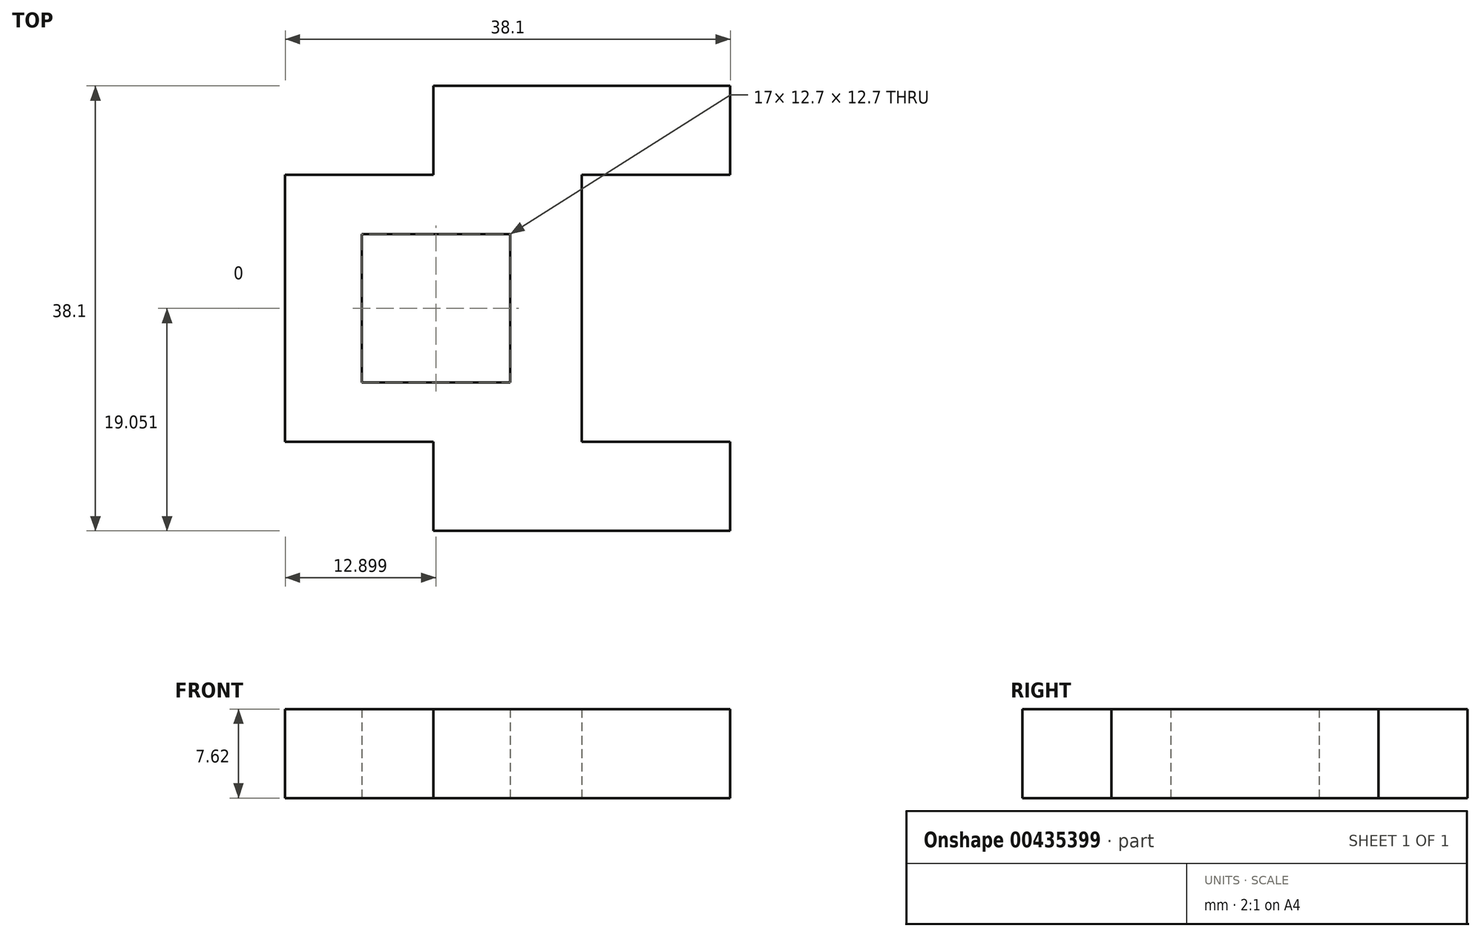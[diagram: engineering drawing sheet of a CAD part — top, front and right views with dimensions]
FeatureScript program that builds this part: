
annotation { "Feature Type Name" : "Feature", "Feature Type Description" : "" }
export const myFeature = defineFeature(function(context is Context, id is Id, definition is map)
    precondition{}
    {
        {
            var Q0;
            Q0=qCreatedBy(makeId("Top.planeOp"),FACE);
            var sketch = newSketch(context, id + "F0", { "sketchPlane" : qUnion([Q0])});
            skLineSegment(sketch, "E0.bottom", {"start": v(-69.04, 57.88) * mm, "end": v(-56.34, 57.88) * mm});
            skLineSegment(sketch, "E0.top", {"start": v(-69.04, 19.78) * mm, "end": v(-56.34, 19.78) * mm});
            skLineSegment(sketch, "E0.left", {"start": v(-69.04, 57.88) * mm, "end": v(-69.04, 45.18) * mm});
            skLineSegment(sketch, "E0.right", {"start": v(-56.34, 57.88) * mm, "end": v(-56.34, 19.78) * mm});
            skLineSegment(sketch, "E1.bottom", {"start": v(-56.34, 57.88) * mm, "end": v(-43.64, 57.88) * mm});
            skLineSegment(sketch, "E1.top", {"start": v(-56.34, 50.26) * mm, "end": v(-43.64, 50.26) * mm});
            skLineSegment(sketch, "E1.left", {"start": v(-56.34, 57.88) * mm, "end": v(-56.34, 50.26) * mm});
            skLineSegment(sketch, "E1.right", {"start": v(-43.64, 57.88) * mm, "end": v(-43.64, 50.26) * mm});
            skLineSegment(sketch, "E2.bottom", {"start": v(-56.34, 19.78) * mm, "end": v(-43.64, 19.78) * mm});
            skLineSegment(sketch, "E2.top", {"start": v(-56.34, 27.4) * mm, "end": v(-43.64, 27.4) * mm});
            skLineSegment(sketch, "E2.left", {"start": v(-56.34, 19.78) * mm, "end": v(-56.34, 27.4) * mm});
            skLineSegment(sketch, "E2.right", {"start": v(-43.64, 19.78) * mm, "end": v(-43.64, 27.4) * mm});
            skLineSegment(sketch, "E3.bottom", {"start": v(-69.04, 50.26) * mm, "end": v(-81.74, 50.26) * mm});
            skLineSegment(sketch, "E3.top", {"start": v(-69.04, 27.4) * mm, "end": v(-81.74, 27.4) * mm});
            skLineSegment(sketch, "E3.left", {"start": v(-69.04, 50.26) * mm, "end": v(-69.04, 45.18) * mm});
            skLineSegment(sketch, "E3.right", {"start": v(-81.74, 50.26) * mm, "end": v(-81.74, 27.4) * mm});
            skLineSegment(sketch, "E4.bottom", {"start": v(-75.2, 45.18) * mm, "end": v(-62.5, 45.18) * mm});
            skLineSegment(sketch, "E4.top", {"start": v(-75.2, 32.48) * mm, "end": v(-62.5, 32.48) * mm});
            skLineSegment(sketch, "E4.left", {"start": v(-75.2, 45.18) * mm, "end": v(-75.2, 45.18) * mm});
            skLineSegment(sketch, "E4.right", {"start": v(-62.5, 45.18) * mm, "end": v(-62.5, 32.48) * mm});
            skLineSegment(sketch, "E5", {"start": v(-75.2, 45.18) * mm, "end": v(-75.2, 32.48) * mm});
            skLineSegment(sketch, "E6.trimOffspring", {"start": v(-69.04, 32.48) * mm, "end": v(-69.04, 19.78) * mm});
            skLineSegment(sketch, "E7.trimOffspring", {"start": v(-69.04, 32.48) * mm, "end": v(-69.04, 27.4) * mm});
            skLineSegment(sketch, "E8", {"start": v(-62.5, 45.18) * mm, "end": v(-56.34, 45.18) * mm});
            skLineSegment(sketch, "E9", {"start": v(-62.5, 32.48) * mm, "end": v(-56.34, 32.48) * mm});
            skSolve(sketch);
        }
        {
            var Q0;
            {var subQ5=sQuery(id+"F0.wireOp",EDGE,"E3.bottom");Q0=makeQuery(id+"F0.imprint","IMPRINT",FACE,{"disambiguationData":[TD([[makeQuery(id+"F0.imprint","IMPRINT",EDGE,{"derivedFrom":subQ5}),1.0]])]});}
            var Q1;
            {var subQ9=sQuery(id+"F0.wireOp",EDGE,"E0.bottom");Q1=makeQuery(id+"F0.imprint","IMPRINT",FACE,{"disambiguationData":[TD([[makeQuery(id+"F0.imprint","IMPRINT",EDGE,{"derivedFrom":subQ9}),-1.0]])]});}
            var Q2;
            Q2=makeQuery(id+"F0.imprint","IMPRINT",FACE,{"disambiguationData":[TD([[makeQuery(id+"F0.imprint","IMPRINT",EDGE,{"derivedFrom":sQuery(id+"F0.wireOp",EDGE,"E1.bottom")}),-1.0]])]});
            var Q3;
            Q3=makeQuery(id+"F0.imprint","IMPRINT",FACE,{"disambiguationData":[TD([[makeQuery(id+"F0.imprint","IMPRINT",EDGE,{"derivedFrom":sQuery(id+"F0.wireOp",EDGE,"E2.bottom")}),1.0]])]});
            var Q4;
            Q4=makeQuery(id+"F0.imprint","IMPRINT",FACE,{"disambiguationData":[TD([[makeQuery(id+"F0.imprint","IMPRINT",EDGE,{"derivedFrom":sQuery(id+"F0.wireOp",EDGE,"E0.top")}),1.0]])]});
            var Q5;
            Q5=makeQuery(id+"F0.imprint","IMPRINT",FACE,{"disambiguationData":[TD([[makeQuery(id+"F0.imprint","IMPRINT",EDGE,{"derivedFrom":sQuery(id+"F0.wireOp",EDGE,"E4.right")}),1.0]])]});
            extrude(context, id + "F1", {"entities" : qUnion([Q0, Q1, Q2, Q3, Q4, Q5]), "depth" : 7.62 * mm});
        }
        {
            var Q0;
            Q0=qCreatedBy(makeId("Top.planeOp"),FACE);
            var sketch = newSketch(context, id + "F2", { "sketchPlane" : qUnion([Q0])});
            skCircle(sketch, "E10", {"center": v(41.2, 17.81) * mm, "radius": 25.4 * mm});
            skSolve(sketch);
        }
        {
            var Q0;
            Q0=makeQuery(id+"F2.imprint","IMPRINT",FACE,{"disambiguationData":[TD([[makeQuery(id+"F2.imprint","IMPRINT",EDGE,{"derivedFrom":sQuery(id+"F2.wireOp",EDGE,"E10")}),1.0]])]});
            extrude(context, id + "F3", {"entities" : qUnion([Q0]), "depth" : 25.4 * mm});
        }
        {
            var Q0;
            Q0=qCreatedBy(makeId("Top.planeOp"),FACE);
            var sketch = newSketch(context, id + "F4", { "sketchPlane" : qUnion([Q0])});
            skCircle(sketch, "E11.cCircle", {"center": v(32.17, 53.94) * mm, "radius": 5.32 * mm, "construction": true});
            skLineSegment(sketch, "E11.0", {"start": v(27.9, 63.67) * mm, "end": v(42.74, 52.77) * mm});
            skLineSegment(sketch, "E11.1", {"start": v(42.74, 52.77) * mm, "end": v(25.88, 45.37) * mm});
            skLineSegment(sketch, "E11.2", {"start": v(25.88, 45.37) * mm, "end": v(27.9, 63.67) * mm});
            skPoint(sketch, "E11.0.midPoint", {"position": v(35.31, 58.22) * mm});
            skSolve(sketch);
        }
        {
            var Q0;
            Q0=makeQuery(id+"F4.imprint","IMPRINT",FACE,{"disambiguationData":[TD([[makeQuery(id+"F4.imprint","IMPRINT",EDGE,{"derivedFrom":sQuery(id+"F4.wireOp",EDGE,"E11.0")}),-1.0]])]});
            extrude(context, id + "F5", {"entities" : qUnion([Q0]), "depth" : 25.4 * mm});
        }
        {
            var Q0;
            Q0=makeQuery(id+"F5.opExtrude","CAP_EDGE",EDGE,{"disambiguationData":[OSD([sQuery(id+"F4.wireOp",EDGE,"E11.0")])],"isStart":false});
            var Q1;
            Q1=makeQuery(id+"F5.opExtrude","CAP_EDGE",EDGE,{"disambiguationData":[OSD([sQuery(id+"F4.wireOp",EDGE,"E11.2")])],"isStart":false});
            var Q2;
            Q2=makeQuery(id+"F5.opExtrude","CAP_EDGE",EDGE,{"disambiguationData":[OSD([sQuery(id+"F4.wireOp",EDGE,"E11.1")])],"isStart":false});
            var Q3;
            Q3=makeQuery(id+"F5.opExtrude","CAP_EDGE",EDGE,{"disambiguationData":[OSD([sQuery(id+"F4.wireOp",EDGE,"E11.0")])],"isStart":true});
            var Q4;
            Q4=makeQuery(id+"F5.opExtrude","CAP_EDGE",EDGE,{"disambiguationData":[OSD([sQuery(id+"F4.wireOp",EDGE,"E11.2")])],"isStart":true});
            var Q5;
            Q5=makeQuery(id+"F5.opExtrude","CAP_EDGE",EDGE,{"disambiguationData":[OSD([sQuery(id+"F4.wireOp",EDGE,"E11.1")])],"isStart":true});
            fillet(context, id + "F6", {"entities" : qUnion([Q0, Q1, Q2, Q3, Q4, Q5]), "radius" : 5.08 * mm, "tangentPropagation" : true, "allowEdgeOverflow" : false});
        }
        {
            var Q0;
            Q0=makeQuery(id+"F5.opExtrude","SWEPT_BODY",BODY,{"disambiguationData":[OSD([sQuery(id+"F4.wireOp",EDGE,"E11.0"),sQuery(id+"F4.wireOp",EDGE,"E11.1"),sQuery(id+"F4.wireOp",EDGE,"E11.2")])]});
            deleteBodies(context, id + "F7", {"entities" : qUnion([Q0])});
        }
        {
            var Q0;
            Q0=makeQuery(id+"F3.opExtrude","SWEPT_BODY",BODY,{"disambiguationData":[OSD([sQuery(id+"F2.wireOp",EDGE,"E10")])]});
            deleteBodies(context, id + "F8", {"entities" : qUnion([Q0])});
        }
    });
